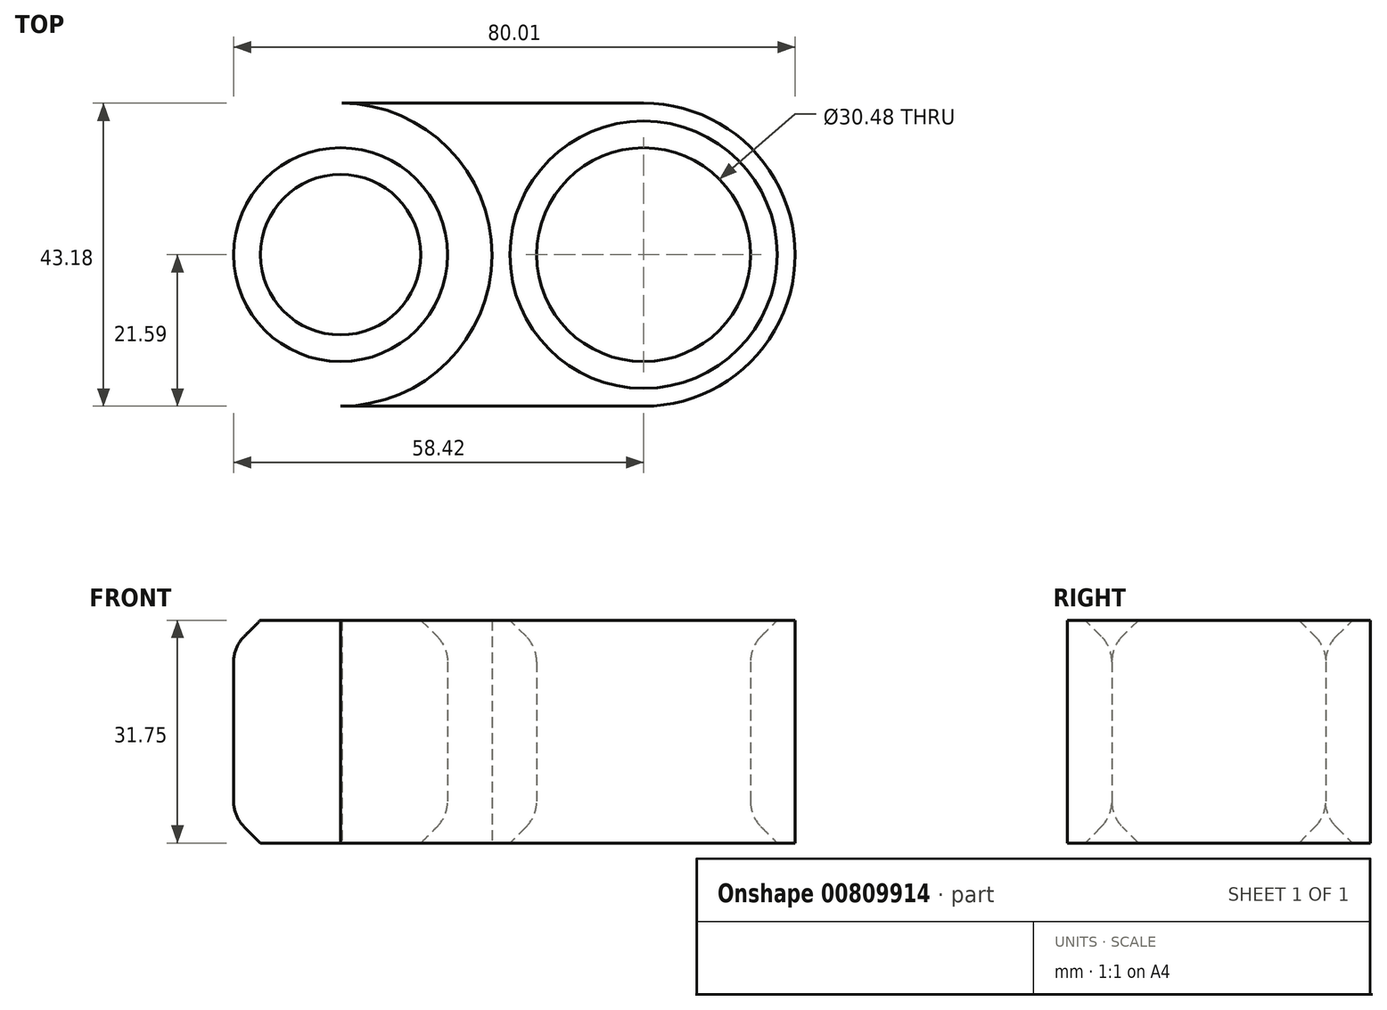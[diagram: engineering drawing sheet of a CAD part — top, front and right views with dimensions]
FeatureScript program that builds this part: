
annotation { "Feature Type Name" : "Feature", "Feature Type Description" : "" }
export const myFeature = defineFeature(function(context is Context, id is Id, definition is map)
    precondition{}
    {
        {
            var Q0;
            Q0=qCreatedBy(makeId("Top.planeOp"),FACE);
            var sketch = newSketch(context, id + "F0", { "sketchPlane" : qUnion([Q0])});
            skCircle(sketch, "E0", {"center": v(19.05, 0) * mm, "radius": 15.24 * mm});
            skCircle(sketch, "E1.0", {"center": v(19.05, 0) * mm, "radius": 21.6 * mm});
            skCircle(sketch, "E2.MirrorC", {"center": v(-24.13, 0) * mm, "radius": 15.24 * mm});
            skCircle(sketch, "E3.MirrorC", {"center": v(-24.13, 0) * mm, "radius": 21.6 * mm});
            skLineSegment(sketch, "E4", {"start": v(-24.13, -21.6) * mm, "end": v(19.05, -21.6) * mm});
            skPoint(sketch, "E5.end.orphan", {"position": v(-2.54, 0) * mm});
            skPoint(sketch, "E6.end.orphan", {"position": v(0, 21.6) * mm});
            skLineSegment(sketch, "E7", {"start": v(-23.94, 21.59) * mm, "end": v(19.05, 21.59) * mm});
            skSolve(sketch);
        }
        {
            var Q0;
            Q0=makeQuery(id+"F0.imprint","IMPRINT",FACE,{"disambiguationData":[TD([[makeQuery(id+"F0.imprint","IMPRINT",EDGE,{"derivedFrom":sQuery(id+"F0.wireOp",EDGE,"E0")}),-1.0]])]});
            var Q1;
            {var subQ0=sQuery(id+"F0.wireOp",EDGE,"c610628f-656b-495e-8c13-aff918d9baef0.MirrorCS");Q1=makeQuery(id+"F0.imprint","IMPRINT",FACE,{"disambiguationData":[TD([[makeQuery(id+"F0.imprint","IMPRINT",EDGE,{"derivedFrom":subQ0}),1.0]])]});}
            var Q2;
            {var subQ0=sQuery(id+"F0.wireOp",EDGE,"E4");Q2=makeQuery(id+"F0.imprint","IMPRINT",FACE,{"disambiguationData":[TD([[makeQuery(id+"F0.imprint","IMPRINT",EDGE,{"derivedFrom":subQ0}),1.0]])]});}
            var Q3;
            Q3=makeQuery(id+"F0.imprint","IMPRINT",FACE,{"disambiguationData":[TD([[makeQuery(id+"F0.imprint","IMPRINT",EDGE,{"derivedFrom":sQuery(id+"F0.wireOp",EDGE,"E2.MirrorC")}),1.0]])]});
            var Q4;
            {var subQ0=sQuery(id+"F0.wireOp",EDGE,"E7");Q4=makeQuery(id+"F0.imprint","IMPRINT",FACE,{"disambiguationData":[TD([[makeQuery(id+"F0.imprint","IMPRINT",EDGE,{"derivedFrom":subQ0}),-1.0]])]});}
            extrude(context, id + "F1", {"entities" : qUnion([Q0, Q1, Q2, Q3, Q4]), "depth" : 31.75 * mm, "offsetDistance" : 25.4 * mm});
        }
        {
            var Q0;
            Q0=makeQuery(id+"F1.opExtrude","CAP_EDGE",EDGE,{"disambiguationData":[OSD([sQuery(id+"F0.wireOp",EDGE,"E2.MirrorC")])],"isStart":true});
            var Q1;
            Q1=makeQuery(id+"F1.opExtrude","CAP_EDGE",EDGE,{"disambiguationData":[OSD([sQuery(id+"F0.wireOp",EDGE,"E0")])],"isStart":true});
            var Q2;
            Q2=makeQuery(id+"F1.opExtrude","CAP_EDGE",EDGE,{"disambiguationData":[OSD([sQuery(id+"F0.wireOp",EDGE,"E0")])],"isStart":false});
            var Q3;
            Q3=makeQuery(id+"F1.opExtrude","CAP_EDGE",EDGE,{"disambiguationData":[OSD([sQuery(id+"F0.wireOp",EDGE,"E2.MirrorC")])],"isStart":false});
            chamfer(context, id + "F2", {"entities" : qUnion([Q0, Q1, Q2, Q3]), "width" : 3.8 * mm, "tangentPropagation" : true});
        }
        {
            var Q0;
            {var subQ0=sQuery(id+"F0.wireOp",EDGE,"E2.MirrorC");Q0=makeQuery(id+"F2.opChamfer","BLEND_EDGE",EDGE,{"blendedFrom":[makeQuery(id+"F1.opExtrude","CAP_EDGE",EDGE,{"disambiguationData":[OSD([subQ0])],"isStart":true}),makeQuery(id+"F1.opExtrude","SWEPT_FACE",FACE,{"disambiguationData":[OSD([subQ0])]})],"blendedInto":[makeQuery(id+"F1.opExtrude","SWEPT_FACE",FACE,{"disambiguationData":[OSD([subQ0])]})]});}
            var Q1;
            {var subQ0=sQuery(id+"F0.wireOp",EDGE,"E2.MirrorC");Q1=makeQuery(id+"F2.opChamfer","BLEND_EDGE",EDGE,{"blendedFrom":[makeQuery(id+"F1.opExtrude","CAP_EDGE",EDGE,{"disambiguationData":[OSD([subQ0])],"isStart":false}),makeQuery(id+"F1.opExtrude","SWEPT_FACE",FACE,{"disambiguationData":[OSD([subQ0])]})],"blendedInto":[makeQuery(id+"F1.opExtrude","SWEPT_FACE",FACE,{"disambiguationData":[OSD([subQ0])]})]});}
            var Q2;
            {var subQ0=sQuery(id+"F0.wireOp",EDGE,"E0");Q2=makeQuery(id+"F2.opChamfer","BLEND_EDGE",EDGE,{"blendedFrom":[makeQuery(id+"F1.opExtrude","CAP_EDGE",EDGE,{"disambiguationData":[OSD([subQ0])],"isStart":false}),makeQuery(id+"F1.opExtrude","SWEPT_FACE",FACE,{"disambiguationData":[OSD([subQ0])]})],"blendedInto":[makeQuery(id+"F1.opExtrude","SWEPT_FACE",FACE,{"disambiguationData":[OSD([subQ0])]})]});}
            var Q3;
            {var subQ0=sQuery(id+"F0.wireOp",EDGE,"E0");Q3=makeQuery(id+"F2.opChamfer","BLEND_EDGE",EDGE,{"blendedFrom":[makeQuery(id+"F1.opExtrude","CAP_EDGE",EDGE,{"disambiguationData":[OSD([subQ0])],"isStart":true}),makeQuery(id+"F1.opExtrude","SWEPT_FACE",FACE,{"disambiguationData":[OSD([subQ0])]})],"blendedInto":[makeQuery(id+"F1.opExtrude","SWEPT_FACE",FACE,{"disambiguationData":[OSD([subQ0])]})]});}
            fillet(context, id + "F3", {"entities" : qUnion([Q0, Q1, Q2, Q3]), "radius" : 5.08 * mm, "tangentPropagation" : true, "allowEdgeOverflow" : false});
        }
    });
